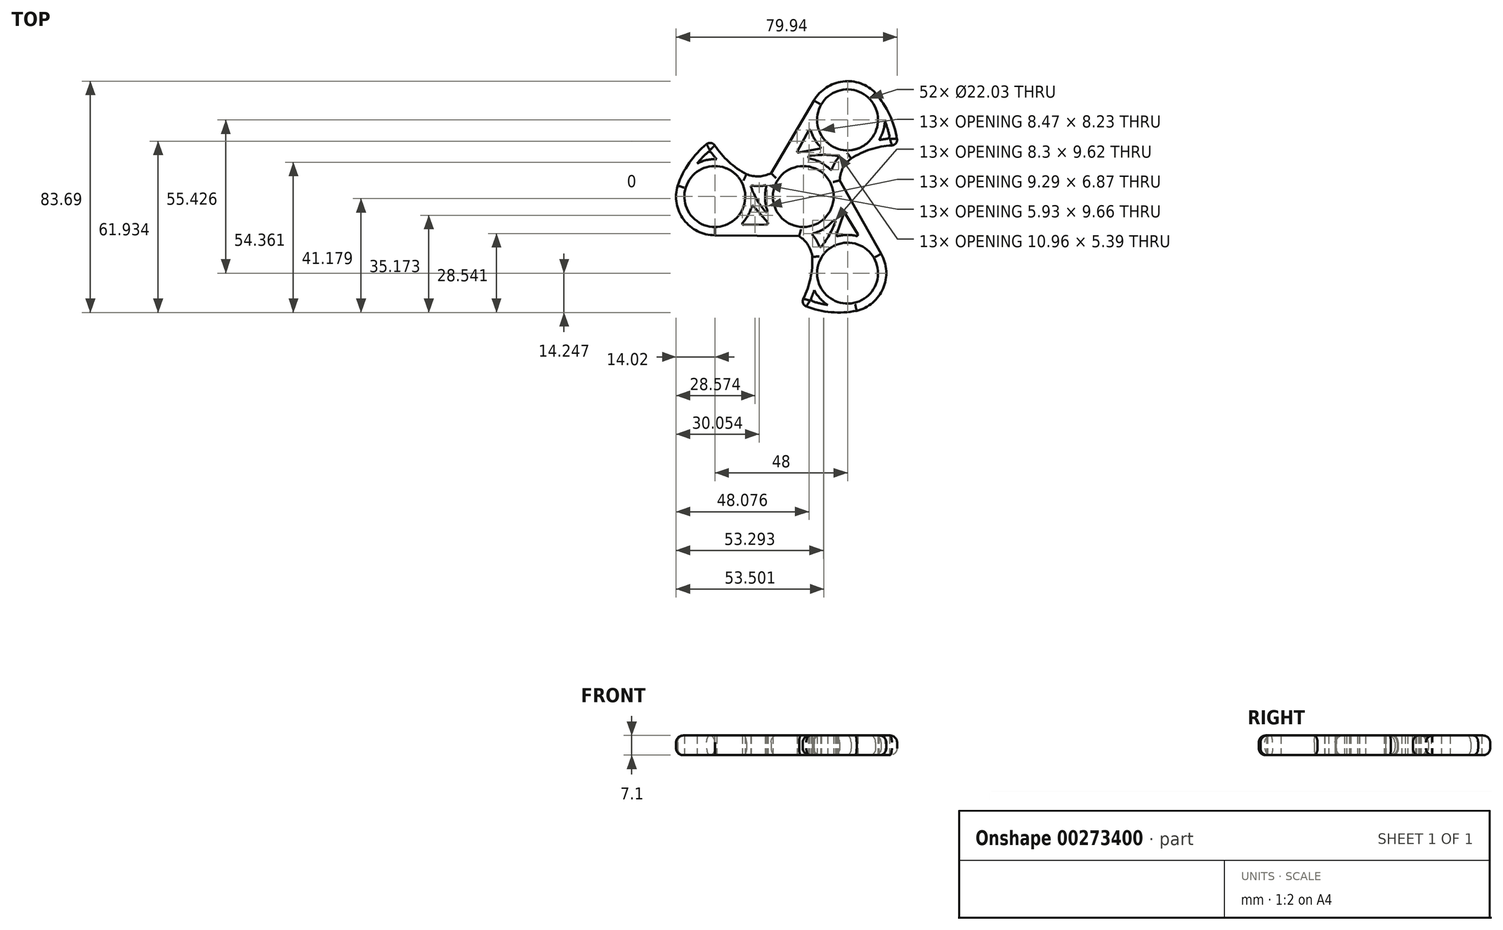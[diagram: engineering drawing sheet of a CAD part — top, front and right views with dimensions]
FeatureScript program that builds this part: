
annotation { "Feature Type Name" : "Feature", "Feature Type Description" : "" }
export const myFeature = defineFeature(function(context is Context, id is Id, definition is map)
    precondition{}
    {
        {
            var Q0;
            Q0=qCreatedBy(makeId("Top.planeOp"),FACE);
            var sketch = newSketch(context, id + "F0", { "sketchPlane" : qUnion([Q0])});
            skCircle(sketch, "E0", {"center": v(0, 0) * mm, "radius": 11.02 * mm});
            skCircle(sketch, "E1", {"center": v(16, 27.71) * mm, "radius": 11.02 * mm});
            skLineSegment(sketch, "E2", {"start": v(0, 0) * mm, "end": v(16, 27.71) * mm, "construction": true});
            skLineSegment(sketch, "E3", {"start": v(16, 27.71) * mm, "end": v(3.86, 34.72) * mm, "construction": true});
            skPoint(sketch, "E4.visualSharp", {"position": v(9, 15.58) * mm});
            skLineSegment(sketch, "E5", {"start": v(16, 27.71) * mm, "end": v(28.14, 20.7) * mm, "construction": true});
            skArc(sketch, "E6", {"start": v(2.75, 23.79) * mm, "mid": v(4.1, 20.69) * mm, "end": v(6.17, 18) * mm});
            skPoint(sketch, "E7.center", {"position": v(-0.23, 0.06) * mm});
            skLineSegment(sketch, "E8", {"start": v(5.94, 17.3) * mm, "end": v(-1.68, 15.87) * mm});
            skPoint(sketch, "E9.orphan", {"position": v(9.2, 15.94) * mm});
            skPoint(sketch, "E10.1.5", {"position": v(0.06, -0.23) * mm});
            skPoint(sketch, "E10.2.5", {"position": v(0.17, 0.17) * mm});
            skLineSegment(sketch, "E11", {"start": v(1.98, 23.87) * mm, "end": v(-2.13, 16.49) * mm});
            skArc(sketch, "E12", {"start": v(12.66, 13.98) * mm, "mid": v(11.36, 12.1) * mm, "end": v(10.44, 10) * mm});
            skArc(sketch, "E13", {"start": v(9.74, 9.82) * mm, "mid": v(6.22, 12.36) * mm, "end": v(2.13, 13.8) * mm});
            skPoint(sketch, "E14.orphan", {"position": v(2.3, 25.96) * mm});
            skArc(sketch, "E15.filletArc", {"start": v(-2.13, 16.49) * mm, "mid": v(-2.1, 16.03) * mm, "end": v(-1.68, 15.87) * mm});
            skPoint(sketch, "E16.visualSharp", {"position": v(10.24, 9.32) * mm});
            skArc(sketch, "E16.filletArc", {"start": v(9.74, 9.82) * mm, "mid": v(10.14, 9.72) * mm, "end": v(10.44, 10) * mm});
            skPoint(sketch, "E17.visualSharp", {"position": v(13.18, 14.57) * mm});
            skArc(sketch, "E17.filletArc", {"start": v(12.66, 13.98) * mm, "mid": v(12.73, 14.4) * mm, "end": v(12.38, 14.67) * mm});
            skArc(sketch, "E18.filletArc", {"start": v(2.16, 14.64) * mm, "mid": v(1.8, 14.24) * mm, "end": v(2.13, 13.8) * mm});
            skPoint(sketch, "E19.visualSharp", {"position": v(6.76, 17.44) * mm});
            skArc(sketch, "E19.filletArc", {"start": v(5.94, 17.3) * mm, "mid": v(6.27, 17.58) * mm, "end": v(6.17, 18) * mm});
            skPoint(sketch, "E20.visualSharp", {"position": v(2.5, 24.8) * mm});
            skArc(sketch, "E20.filletArc", {"start": v(2.75, 23.79) * mm, "mid": v(2.4, 24.09) * mm, "end": v(1.98, 23.87) * mm});
            skArc(sketch, "E21", {"start": v(12.38, 14.67) * mm, "mid": v(7.27, 15.1) * mm, "end": v(2.16, 14.64) * mm});
            skArc(sketch, "E22", {"start": v(17.28, 13.76) * mm, "mid": v(14.34, 10.27) * mm, "end": v(13.18, 5.86) * mm});
            skLineSegment(sketch, "E23.1.1", {"start": v(-11.67, 8.49) * mm, "end": v(3.86, 34.72) * mm});
            skArc(sketch, "E24.1.0", {"start": v(-45.45, 3.95) * mm, "mid": v(-43.22, -8.4) * mm, "end": v(-32, -14.01) * mm});
            skPoint(sketch, "E24.1.1", {"position": v(-23.63, -11) * mm});
            skPoint(sketch, "E24.1.2", {"position": v(-13.2, 4.2) * mm});
            skLineSegment(sketch, "E24.1.3", {"start": v(-1.51, -14.35) * mm, "end": v(-32, -14.01) * mm});
            skArc(sketch, "E24.1.4", {"start": v(-20.55, 8.08) * mm, "mid": v(-16.06, 7.28) * mm, "end": v(-11.67, 8.49) * mm});
            skCircle(sketch, "E24.1.5", {"center": v(-32, 0) * mm, "radius": 11.02 * mm});
            skPoint(sketch, "E24.1.6", {"position": v(-19.2, 4.13) * mm});
            skPoint(sketch, "E24.1.7", {"position": v(-17.98, 0) * mm});
            skArc(sketch, "E24.1.8", {"start": v(-21.98, -9.5) * mm, "mid": v(-19.97, -6.79) * mm, "end": v(-18.68, -3.66) * mm});
            skLineSegment(sketch, "E24.1.9", {"start": v(-21.66, -10.22) * mm, "end": v(-13.22, -10.09) * mm});
            skArc(sketch, "E24.1.10", {"start": v(-13.38, 3.53) * mm, "mid": v(-13.82, -0.8) * mm, "end": v(-13.02, -5.06) * mm});
            skArc(sketch, "E24.1.11", {"start": v(-18.9, 3.39) * mm, "mid": v(-16.71, -1.25) * mm, "end": v(-13.76, -5.45) * mm});
            skPoint(sketch, "E24.1.12", {"position": v(-18.4, 0) * mm});
            skLineSegment(sketch, "E24.1.13", {"start": v(-17.95, -3.5) * mm, "end": v(-12.9, -9.39) * mm});
            skPoint(sketch, "E24.1.14", {"position": v(-18.49, -2.87) * mm});
            skPoint(sketch, "E24.1.15", {"position": v(-22.73, -10.24) * mm});
            skArc(sketch, "E24.1.16", {"start": v(-18.44, 3.97) * mm, "mid": v(-18.84, 3.82) * mm, "end": v(-18.9, 3.39) * mm});
            skArc(sketch, "E24.1.17", {"start": v(-18.44, 3.97) * mm, "mid": v(-16.15, 3.8) * mm, "end": v(-13.88, 4.04) * mm});
            skArc(sketch, "E24.1.18", {"start": v(-13.22, -10.09) * mm, "mid": v(-12.84, -9.84) * mm, "end": v(-12.9, -9.39) * mm});
            skArc(sketch, "E24.1.19", {"start": v(-21.98, -9.5) * mm, "mid": v(-22.06, -9.97) * mm, "end": v(-21.66, -10.22) * mm});
            skArc(sketch, "E24.1.20", {"start": v(-13.38, 3.53) * mm, "mid": v(-13.48, 3.92) * mm, "end": v(-13.88, 4.04) * mm});
            skArc(sketch, "E24.1.21", {"start": v(-13.76, -5.45) * mm, "mid": v(-13.23, -5.57) * mm, "end": v(-13.02, -5.06) * mm});
            skArc(sketch, "E24.1.22", {"start": v(-17.95, -3.5) * mm, "mid": v(-18.36, -3.36) * mm, "end": v(-18.68, -3.66) * mm});
            skPoint(sketch, "E24.2.1", {"position": v(21.34, -14.97) * mm});
            skPoint(sketch, "E24.2.2", {"position": v(2.95, -13.53) * mm});
            skLineSegment(sketch, "E24.2.3", {"start": v(13.18, 5.86) * mm, "end": v(28.14, -20.7) * mm});
            skArc(sketch, "E24.2.4", {"start": v(3.28, -21.84) * mm, "mid": v(1.72, -17.55) * mm, "end": v(-1.51, -14.35) * mm});
            skCircle(sketch, "E24.2.5", {"center": v(16, -27.71) * mm, "radius": 11.02 * mm});
            skPoint(sketch, "E24.2.6", {"position": v(6.03, -18.7) * mm});
            skPoint(sketch, "E24.2.7", {"position": v(9, -15.58) * mm});
            skArc(sketch, "E24.2.8", {"start": v(19.22, -14.28) * mm, "mid": v(15.86, -13.9) * mm, "end": v(12.51, -14.35) * mm});
            skLineSegment(sketch, "E24.2.9", {"start": v(19.68, -13.65) * mm, "end": v(15.34, -6.4) * mm});
            skArc(sketch, "E24.2.10", {"start": v(3.64, -13.35) * mm, "mid": v(7.6, -11.57) * mm, "end": v(10.9, -8.75) * mm});
            skArc(sketch, "E24.2.11", {"start": v(6.52, -18.06) * mm, "mid": v(9.44, -13.85) * mm, "end": v(11.6, -9.2) * mm});
            skPoint(sketch, "E24.2.12", {"position": v(9.2, -15.94) * mm});
            skLineSegment(sketch, "E24.2.13", {"start": v(12, -13.8) * mm, "end": v(14.58, -6.48) * mm});
            skPoint(sketch, "E24.2.14", {"position": v(11.73, -14.57) * mm});
            skPoint(sketch, "E24.2.15", {"position": v(20.23, -14.56) * mm});
            skArc(sketch, "E24.2.16", {"start": v(5.78, -17.95) * mm, "mid": v(6.11, -18.23) * mm, "end": v(6.52, -18.06) * mm});
            skArc(sketch, "E24.2.17", {"start": v(5.78, -17.95) * mm, "mid": v(4.8, -15.88) * mm, "end": v(3.44, -14.04) * mm});
            skArc(sketch, "E24.2.18", {"start": v(15.34, -6.4) * mm, "mid": v(14.94, -6.2) * mm, "end": v(14.58, -6.48) * mm});
            skArc(sketch, "E24.2.19", {"start": v(19.22, -14.28) * mm, "mid": v(19.66, -14.12) * mm, "end": v(19.68, -13.65) * mm});
            skArc(sketch, "E24.2.20", {"start": v(3.64, -13.35) * mm, "mid": v(3.35, -13.64) * mm, "end": v(3.44, -14.04) * mm});
            skArc(sketch, "E24.2.21", {"start": v(11.6, -9.2) * mm, "mid": v(11.43, -8.67) * mm, "end": v(10.9, -8.75) * mm});
            skArc(sketch, "E24.2.22", {"start": v(12, -13.8) * mm, "mid": v(12.1, -14.22) * mm, "end": v(12.51, -14.35) * mm});
            skArc(sketch, "E25.trimOffspring", {"start": v(26.14, 37.38) * mm, "mid": v(14.34, 41.63) * mm, "end": v(3.86, 34.72) * mm});
            skArc(sketch, "E26.trimOffspring", {"start": v(19.3, -41.33) * mm, "mid": v(28.88, -33.23) * mm, "end": v(28.14, -20.7) * mm});
            skArc(sketch, "E27", {"start": v(-32.02, 18.5) * mm, "mid": v(-26.95, 12.56) * mm, "end": v(-20.55, 8.08) * mm});
            skArc(sketch, "E28", {"start": v(-34.95, 18.96) * mm, "mid": v(-41.26, 12.2) * mm, "end": v(-45.45, 3.95) * mm});
            skArc(sketch, "E29.trimOffspring", {"start": v(-33.18, 15.77) * mm, "mid": v(-32.3, 14.62) * mm, "end": v(-31.37, 13.5) * mm});
            skArc(sketch, "E30.trimOffspring", {"start": v(-34.66, 15.93) * mm, "mid": v(-36.6, 14) * mm, "end": v(-38.37, 11.92) * mm});
            skArc(sketch, "E31.trimOffspring", {"start": v(-31.37, 13.5) * mm, "mid": v(-34.97, 13.18) * mm, "end": v(-38.37, 11.92) * mm});
            skPoint(sketch, "E32.visualSharp", {"position": v(-33.13, 20.33) * mm});
            skArc(sketch, "E32.filletArc", {"start": v(-32.02, 18.5) * mm, "mid": v(-33.38, 19.38) * mm, "end": v(-34.95, 18.96) * mm});
            skPoint(sketch, "E33.visualSharp", {"position": v(-33.8, 16.67) * mm});
            skArc(sketch, "E33.filletArc", {"start": v(-33.18, 15.77) * mm, "mid": v(-33.88, 16.18) * mm, "end": v(-34.66, 15.93) * mm});
            skArc(sketch, "E34.1.0", {"start": v(2.93, -36.62) * mm, "mid": v(3.49, -35.28) * mm, "end": v(4, -33.91) * mm});
            skPoint(sketch, "E34.1.1", {"position": v(2.47, -37.6) * mm});
            skArc(sketch, "E34.1.2", {"start": v(4, -33.91) * mm, "mid": v(6.07, -36.88) * mm, "end": v(8.86, -39.19) * mm});
            skArc(sketch, "E34.1.3", {"start": v(3.53, -37.98) * mm, "mid": v(6.17, -38.7) * mm, "end": v(8.86, -39.19) * mm});
            skPoint(sketch, "E34.1.4", {"position": v(-1.04, -38.86) * mm});
            skArc(sketch, "E34.1.5", {"start": v(0.02, -36.6) * mm, "mid": v(0.09, -36.62) * mm, "end": v(0.15, -36.65) * mm});
            skArc(sketch, "E34.1.6", {"start": v(-0.01, -36.98) * mm, "mid": v(-0.1, -38.6) * mm, "end": v(1.05, -39.75) * mm});
            skArc(sketch, "E34.1.7", {"start": v(2.93, -36.62) * mm, "mid": v(2.93, -37.43) * mm, "end": v(3.53, -37.98) * mm});
            skArc(sketch, "E34.1.8", {"start": v(1.05, -39.75) * mm, "mid": v(10.07, -41.83) * mm, "end": v(19.3, -41.33) * mm});
            skArc(sketch, "E34.1.9", {"start": v(-0.01, -36.98) * mm, "mid": v(2.6, -29.62) * mm, "end": v(3.28, -21.84) * mm});
            skArc(sketch, "E34.2.0", {"start": v(30.25, 20.85) * mm, "mid": v(28.8, 20.66) * mm, "end": v(27.37, 20.41) * mm});
            skPoint(sketch, "E34.2.1", {"position": v(31.34, 20.94) * mm});
            skArc(sketch, "E34.2.2", {"start": v(27.37, 20.41) * mm, "mid": v(28.9, 23.7) * mm, "end": v(29.5, 27.27) * mm});
            skArc(sketch, "E34.2.3", {"start": v(31.12, 22.05) * mm, "mid": v(30.43, 24.7) * mm, "end": v(29.5, 27.27) * mm});
            skPoint(sketch, "E34.2.4", {"position": v(34.17, 18.53) * mm});
            skArc(sketch, "E34.2.5", {"start": v(31.68, 18.31) * mm, "mid": v(31.67, 18.39) * mm, "end": v(31.67, 18.46) * mm});
            skArc(sketch, "E34.2.6", {"start": v(32.03, 18.48) * mm, "mid": v(33.48, 19.22) * mm, "end": v(33.9, 20.79) * mm});
            skArc(sketch, "E34.2.7", {"start": v(30.25, 20.85) * mm, "mid": v(30.95, 21.25) * mm, "end": v(31.12, 22.05) * mm});
            skArc(sketch, "E34.2.8", {"start": v(33.9, 20.79) * mm, "mid": v(31.2, 29.63) * mm, "end": v(26.14, 37.38) * mm});
            skArc(sketch, "E34.2.9", {"start": v(32.03, 18.48) * mm, "mid": v(24.35, 17.06) * mm, "end": v(17.28, 13.76) * mm});
            skSolve(sketch);
        }
        {
            var Q0;
            Q0=makeQuery(id+"F0.imprint","IMPRINT",FACE,{"disambiguationData":[TD([[makeQuery(id+"F0.imprint","IMPRINT",EDGE,{"derivedFrom":sQuery(id+"F0.wireOp",EDGE,"ea44153e-c5e4-4200-878d-53ebf284e07f.1.0")}),-1.0]])]});
            var Q1;
            Q1=makeQuery(id+"F0.imprint","IMPRINT",FACE,{"disambiguationData":[TD([[makeQuery(id+"F0.imprint","IMPRINT",EDGE,{"derivedFrom":sQuery(id+"F0.wireOp",EDGE,"E0")}),-1.0]])]});
            var Q2;
            Q2=makeQuery(id+"F0.imprint","IMPRINT",FACE,{"disambiguationData":[TD([[makeQuery(id+"F0.imprint","IMPRINT",EDGE,{"derivedFrom":sQuery(id+"F0.wireOp",EDGE,"E1")}),-1.0]])]});
            var Q3;
            {var subQ0=sQuery(id+"F0.wireOp",EDGE,"zqQpl2xC-KShR-byGl-JfGq-b1LpVGurQPJH");Q3=makeQuery(id+"F0.imprint","IMPRINT",FACE,{"disambiguationData":[TD([[makeQuery(id+"F0.imprint","IMPRINT",EDGE,{"derivedFrom":subQ0}),-1.0]])]});}
            var Q4;
            Q4=makeQuery(id+"F0.imprint","IMPRINT",FACE,{"disambiguationData":[TD([[makeQuery(id+"F0.imprint","IMPRINT",EDGE,{"derivedFrom":sQuery(id+"F0.wireOp",EDGE,"1881bb9a-ca16-43a5-8112-34110b48d62d.0")}),-1.0]])]});
            var Q5;
            Q5=makeQuery(id+"F0.imprint","IMPRINT",FACE,{"disambiguationData":[TD([[makeQuery(id+"F0.imprint","IMPRINT",EDGE,{"derivedFrom":sQuery(id+"F0.wireOp",EDGE,"5a72e3ce-2744-4da3-adbb-3a9f07581b46.2.1")}),1.0]])]});
            var Q6;
            Q6=makeQuery(id+"F0.imprint","IMPRINT",FACE,{"disambiguationData":[TD([[makeQuery(id+"F0.imprint","IMPRINT",EDGE,{"derivedFrom":sQuery(id+"F0.wireOp",EDGE,"5a72e3ce-2744-4da3-adbb-3a9f07581b46.1.1")}),1.0]])]});
            extrude(context, id + "F1", {"entities" : qUnion([Q0, Q1, Q2, Q3, Q4, Q5, Q6]), "depth" : 7.1 * mm});
        }
        {
            var Q0;
            Q0=makeQuery(id+"F1.opExtrude","CAP_EDGE",EDGE,{"disambiguationData":[OSD([sQuery(id+"F0.wireOp",EDGE,"E24.1.3")])],"isStart":true});
            var Q1;
            Q1=makeQuery(id+"F1.opExtrude","CAP_EDGE",EDGE,{"disambiguationData":[OSD([sQuery(id+"F0.wireOp",EDGE,"E23.1.1")])],"isStart":true});
            var Q2;
            Q2=makeQuery(id+"F1.opExtrude","CAP_EDGE",EDGE,{"disambiguationData":[OSD([sQuery(id+"F0.wireOp",EDGE,"E24.2.3")])],"isStart":true});
            var Q3;
            Q3=makeQuery(id+"F1.opExtrude","CAP_EDGE",EDGE,{"disambiguationData":[OSD([sQuery(id+"F0.wireOp",EDGE,"E24.2.3")])],"isStart":false});
            var Q4;
            Q4=makeQuery(id+"F1.opExtrude","CAP_EDGE",EDGE,{"disambiguationData":[OSD([sQuery(id+"F0.wireOp",EDGE,"E24.1.3")])],"isStart":false});
            var Q5;
            Q5=makeQuery(id+"F1.opExtrude","CAP_EDGE",EDGE,{"disambiguationData":[OSD([sQuery(id+"F0.wireOp",EDGE,"E23.1.1")])],"isStart":false});
            var Q6;
            Q6=makeQuery(id+"F1.opExtrude","CAP_EDGE",EDGE,{"disambiguationData":[OSD([sQuery(id+"F0.wireOp",EDGE,"E24.1.3")])],"isStart":false});
            var Q7;
            Q7=makeQuery(id+"F1.opExtrude","CAP_EDGE",EDGE,{"disambiguationData":[OSD([sQuery(id+"F0.wireOp",EDGE,"E23.1.1")])],"isStart":false});
            var Q8;
            Q8=makeQuery(id+"F1.opExtrude","CAP_EDGE",EDGE,{"disambiguationData":[OSD([sQuery(id+"F0.wireOp",EDGE,"E24.2.3")])],"isStart":false});
            var Q9;
            Q9=makeQuery(id+"F1.opExtrude","CAP_EDGE",EDGE,{"disambiguationData":[OSD([sQuery(id+"F0.wireOp",EDGE,"E24.1.3")])],"isStart":false});
            var Q10;
            Q10=makeQuery(id+"F1.opExtrude","CAP_EDGE",EDGE,{"disambiguationData":[OSD([sQuery(id+"F0.wireOp",EDGE,"E24.2.3")])],"isStart":false});
            var Q11;
            Q11=makeQuery(id+"F1.opExtrude","CAP_EDGE",EDGE,{"disambiguationData":[OSD([sQuery(id+"F0.wireOp",EDGE,"E23.1.1")])],"isStart":false});
            var Q12;
            Q12=makeQuery(id+"F1.opExtrude","CAP_EDGE",EDGE,{"disambiguationData":[OSD([sQuery(id+"F0.wireOp",EDGE,"E26.trimOffspring")])],"isStart":false});
            var Q13;
            Q13=makeQuery(id+"F1.opExtrude","CAP_EDGE",EDGE,{"disambiguationData":[OSD([sQuery(id+"F0.wireOp",EDGE,"E24.1.0")])],"isStart":false});
            var Q14;
            Q14=makeQuery(id+"F1.opExtrude","CAP_EDGE",EDGE,{"disambiguationData":[OSD([sQuery(id+"F0.wireOp",EDGE,"E25.trimOffspring")])],"isStart":false});
            var Q15;
            Q15=makeQuery(id+"F1.opExtrude","CAP_EDGE",EDGE,{"disambiguationData":[OSD([sQuery(id+"F0.wireOp",EDGE,"E24.2.4")])],"isStart":false});
            var Q16;
            Q16=makeQuery(id+"F1.opExtrude","CAP_EDGE",EDGE,{"disambiguationData":[OSD([sQuery(id+"F0.wireOp",EDGE,"E22")])],"isStart":false});
            var Q17;
            Q17=makeQuery(id+"F1.opExtrude","CAP_EDGE",EDGE,{"disambiguationData":[OSD([sQuery(id+"F0.wireOp",EDGE,"E27")])],"isStart":true});
            var Q18;
            Q18=makeQuery(id+"F1.opExtrude","CAP_EDGE",EDGE,{"disambiguationData":[OSD([sQuery(id+"F0.wireOp",EDGE,"E24.1.4")])],"isStart":false});
            var Q19;
            Q19=makeQuery(id+"F1.opExtrude","CAP_EDGE",EDGE,{"disambiguationData":[OSD([sQuery(id+"F0.wireOp",EDGE,"E27")])],"isStart":false});
            var Q20;
            Q20=makeQuery(id+"F1.opExtrude","CAP_EDGE",EDGE,{"disambiguationData":[OSD([sQuery(id+"F0.wireOp",EDGE,"E34.2.9")])],"isStart":false});
            var Q21;
            Q21=makeQuery(id+"F1.opExtrude","CAP_EDGE",EDGE,{"disambiguationData":[OSD([sQuery(id+"F0.wireOp",EDGE,"E34.1.9")])],"isStart":false});
            var Q22;
            Q22=makeQuery(id+"F1.opExtrude","CAP_EDGE",EDGE,{"disambiguationData":[OSD([sQuery(id+"F0.wireOp",EDGE,"E34.2.6")])],"isStart":false});
            var Q23;
            Q23=makeQuery(id+"F1.opExtrude","CAP_EDGE",EDGE,{"disambiguationData":[OSD([sQuery(id+"F0.wireOp",EDGE,"E26.trimOffspring")])],"isStart":true});
            var Q24;
            Q24=makeQuery(id+"F1.opExtrude","CAP_EDGE",EDGE,{"disambiguationData":[OSD([sQuery(id+"F0.wireOp",EDGE,"E34.2.8")])],"isStart":true});
            var Q25;
            Q25=makeQuery(id+"F1.opExtrude","CAP_EDGE",EDGE,{"disambiguationData":[OSD([sQuery(id+"F0.wireOp",EDGE,"E22")])],"isStart":true});
            var Q26;
            Q26=makeQuery(id+"F1.opExtrude","CAP_EDGE",EDGE,{"disambiguationData":[OSD([sQuery(id+"F0.wireOp",EDGE,"E34.2.9")])],"isStart":true});
            var Q27;
            Q27=makeQuery(id+"F1.opExtrude","CAP_EDGE",EDGE,{"disambiguationData":[OSD([sQuery(id+"F0.wireOp",EDGE,"E24.1.0")])],"isStart":true});
            var Q28;
            Q28=makeQuery(id+"F1.opExtrude","CAP_EDGE",EDGE,{"disambiguationData":[OSD([sQuery(id+"F0.wireOp",EDGE,"E34.1.9")])],"isStart":true});
            var Q29;
            Q29=makeQuery(id+"F1.opExtrude","CAP_EDGE",EDGE,{"disambiguationData":[OSD([sQuery(id+"F0.wireOp",EDGE,"E34.1.6")])],"isStart":true});
            var Q30;
            Q30=makeQuery(id+"F1.opExtrude","CAP_EDGE",EDGE,{"disambiguationData":[OSD([sQuery(id+"F0.wireOp",EDGE,"E24.2.4")])],"isStart":true});
            var Q31;
            Q31=makeQuery(id+"F1.opExtrude","CAP_EDGE",EDGE,{"disambiguationData":[OSD([sQuery(id+"F0.wireOp",EDGE,"E25.trimOffspring")])],"isStart":true});
            fillet(context, id + "F2", {"entities" : qUnion([Q0, Q1, Q2, Q3, Q4, Q5, Q6, Q7, Q8, Q9, Q10, Q11, Q12, Q13, Q14, Q15, Q16, Q17, Q18, Q19, Q20, Q21, Q22, Q23, Q24, Q25, Q26, Q27, Q28, Q29, Q30, Q31]), "radius" : 2.5 * mm, "tangentPropagation" : true, "allowEdgeOverflow" : false});
        }
    });
